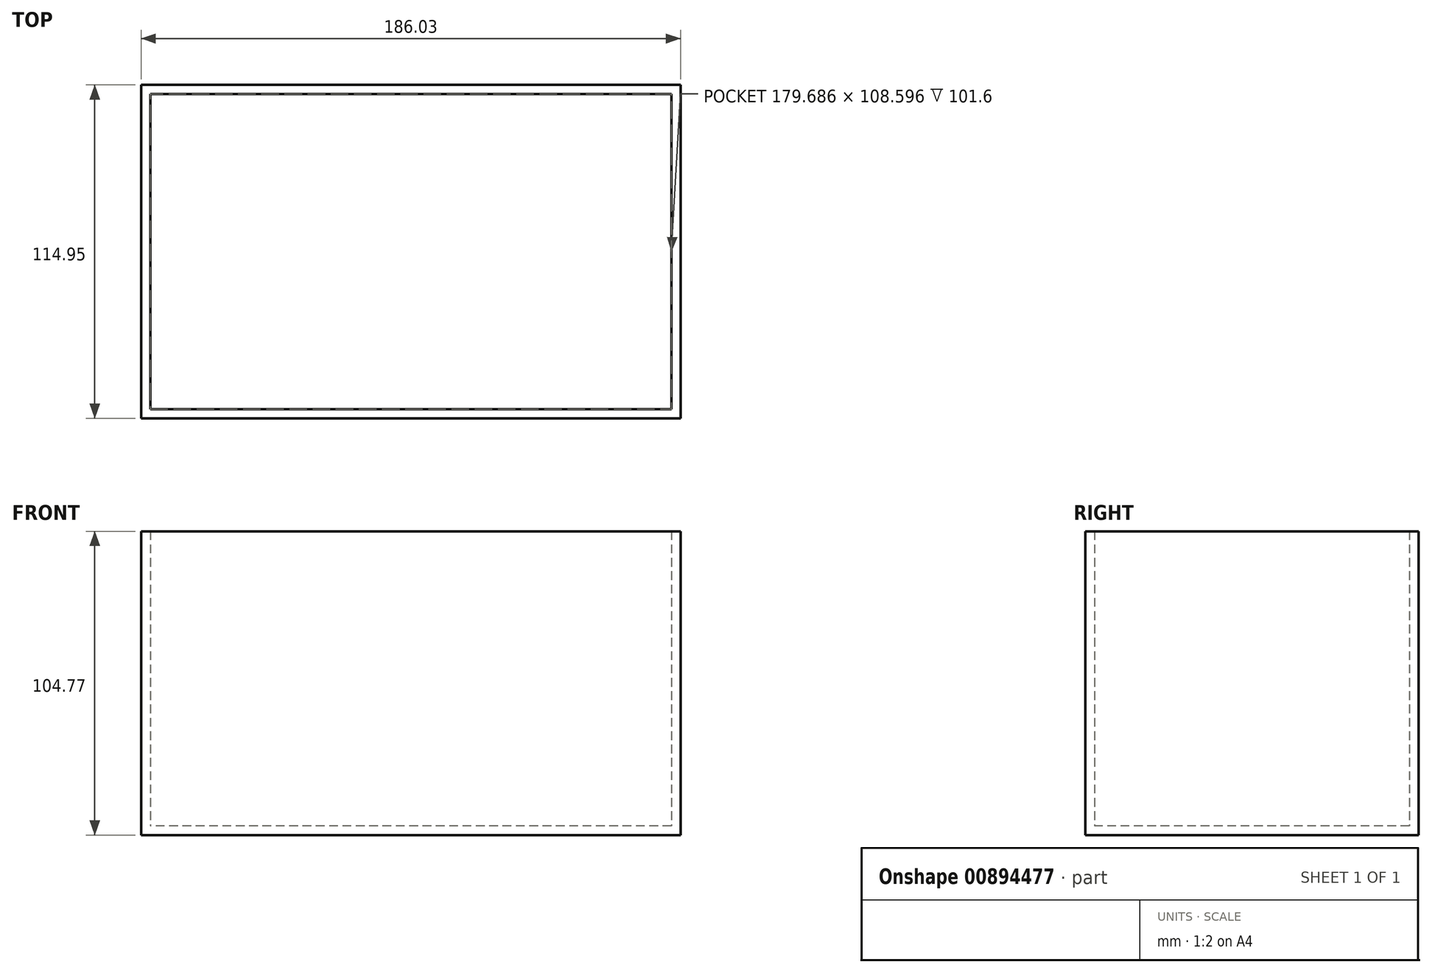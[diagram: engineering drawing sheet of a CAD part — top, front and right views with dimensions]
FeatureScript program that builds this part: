
annotation { "Feature Type Name" : "Feature", "Feature Type Description" : "" }
export const myFeature = defineFeature(function(context is Context, id is Id, definition is map)
    precondition{}
    {
        {
            var Q0;
            Q0=qCreatedBy(makeId("Top.planeOp"),FACE);
            var sketch = newSketch(context, id + "F0", { "sketchPlane" : qUnion([Q0])});
            skLineSegment(sketch, "E0.bottom", {"start": v(125.87, 58.3) * mm, "end": v(-60.16, 58.3) * mm});
            skLineSegment(sketch, "E0.top", {"start": v(125.87, -56.64) * mm, "end": v(-60.16, -56.64) * mm});
            skLineSegment(sketch, "E0.left", {"start": v(125.87, 58.3) * mm, "end": v(125.87, -56.64) * mm});
            skLineSegment(sketch, "E0.right", {"start": v(-60.16, 58.3) * mm, "end": v(-60.16, -56.64) * mm});
            skLineSegment(sketch, "E1", {"start": v(-60.16, -56.64) * mm, "end": v(125.87, 58.3) * mm, "construction": true});
            skSolve(sketch);
        }
        {
            var Q0;
            Q0=makeQuery(id+"F0.imprint","IMPRINT",FACE,{"disambiguationData":[TD([[makeQuery(id+"F0.imprint","IMPRINT",EDGE,{"derivedFrom":sQuery(id+"F0.wireOp",EDGE,"E0.bottom")}),1.0]])]});
            extrude(context, id + "F1", {"entities" : qUnion([Q0]), "depth" : 3.17 * mm, "offsetDistance" : 25.4 * mm});
        }
        {
            var Q0;
            Q0=makeQuery(id+"F1.opExtrude","CAP_FACE",FACE,{"disambiguationData":[OSD([sQuery(id+"F0.wireOp",EDGE,"E0.bottom"),sQuery(id+"F0.wireOp",EDGE,"E0.top"),sQuery(id+"F0.wireOp",EDGE,"E0.left"),sQuery(id+"F0.wireOp",EDGE,"E0.right")])],"isStart":false});
            var sketch = newSketch(context, id + "F2", { "sketchPlane" : qUnion([Q0])});
            skLineSegment(sketch, "E2.bottom", {"start": v(125.87, 58.3) * mm, "end": v(-60.16, 58.3) * mm});
            skLineSegment(sketch, "E2.top", {"start": v(125.87, -56.64) * mm, "end": v(-60.16, -56.64) * mm});
            skLineSegment(sketch, "E2.left", {"start": v(125.87, 58.3) * mm, "end": v(125.87, -56.64) * mm});
            skLineSegment(sketch, "E2.right", {"start": v(-60.16, 58.3) * mm, "end": v(-60.16, -56.64) * mm});
            skLineSegment(sketch, "E3.0", {"start": v(122.7, -53.46) * mm, "end": v(-56.99, -53.46) * mm});
            skLineSegment(sketch, "E3.1", {"start": v(122.7, 55.13) * mm, "end": v(122.7, -53.46) * mm});
            skLineSegment(sketch, "E3.2", {"start": v(122.7, 55.13) * mm, "end": v(-56.99, 55.13) * mm});
            skLineSegment(sketch, "E3.3", {"start": v(-56.99, 55.13) * mm, "end": v(-56.99, -53.46) * mm});
            skSolve(sketch);
        }
        {
            var Q0;
            Q0 = qSketchRegion(id + "F2", true);
            extrude(context, id + "F3", {"entities" : qUnion([Q0]), "operationType" : NewBodyOperationType.ADD, "depth" : 101.6 * mm, "offsetDistance" : 25.4 * mm});
        }
    });
